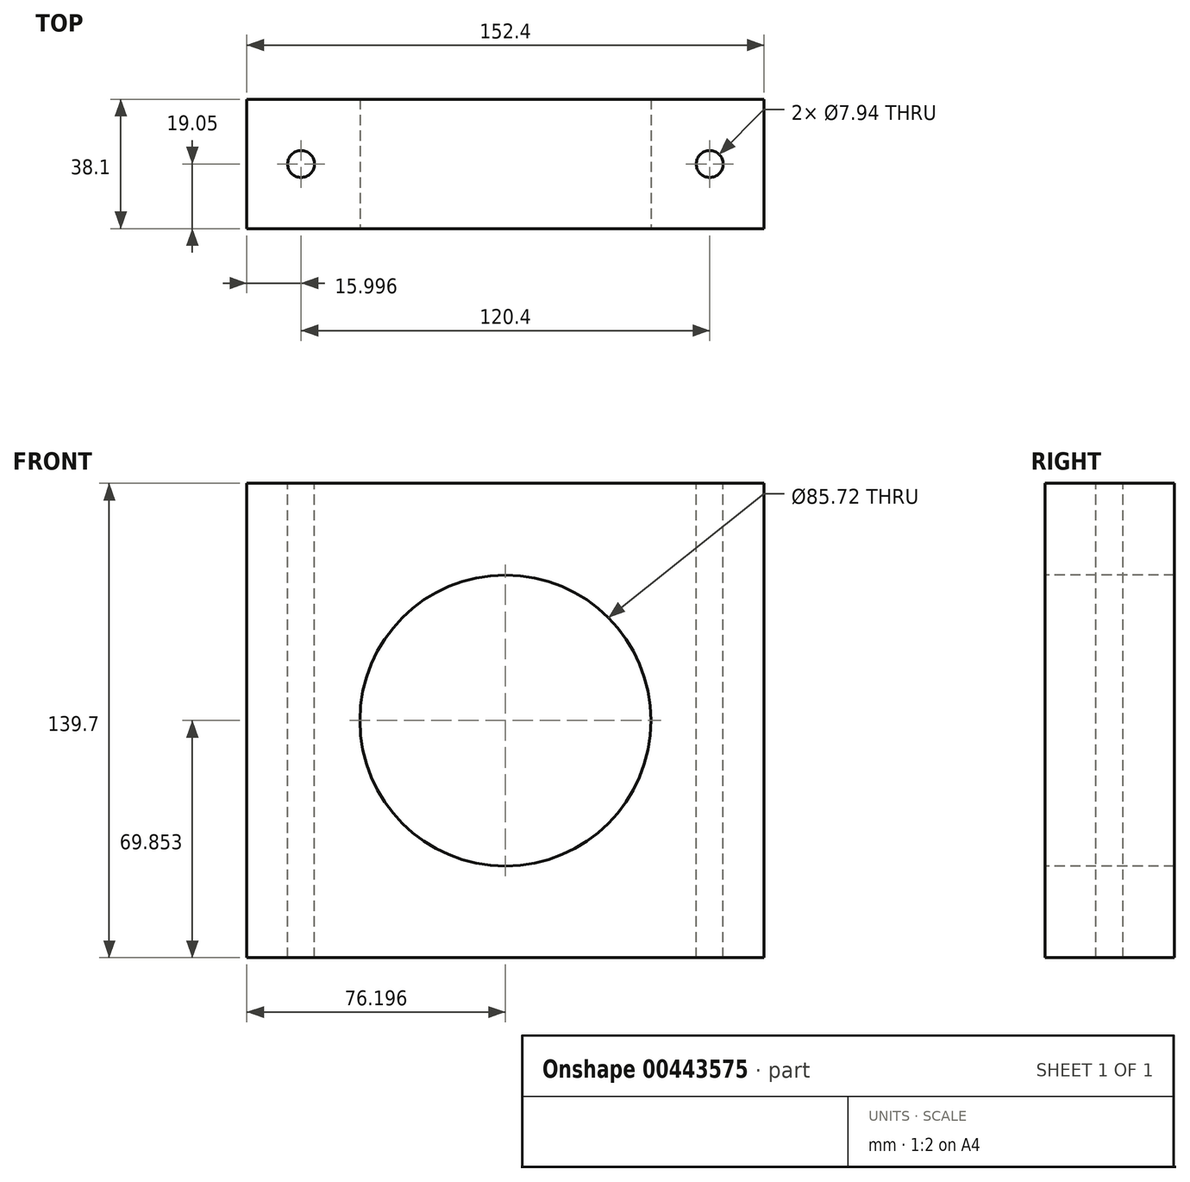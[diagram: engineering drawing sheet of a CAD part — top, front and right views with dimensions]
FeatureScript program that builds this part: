
annotation { "Feature Type Name" : "Feature", "Feature Type Description" : "" }
export const myFeature = defineFeature(function(context is Context, id is Id, definition is map)
    precondition{}
    {
        {
            var Q0;
            Q0=qCreatedBy(makeId("Front.planeOp"),FACE);
            var sketch = newSketch(context, id + "F0", { "sketchPlane" : qUnion([Q0])});
            skLineSegment(sketch, "E0.bottom", {"start": v(-104.36, 73.36) * mm, "end": v(48.04, 73.36) * mm});
            skLineSegment(sketch, "E0.top", {"start": v(-104.36, -66.34) * mm, "end": v(48.04, -66.34) * mm});
            skLineSegment(sketch, "E0.left", {"start": v(-104.36, 73.36) * mm, "end": v(-104.36, -66.34) * mm});
            skLineSegment(sketch, "E0.right", {"start": v(48.04, 73.36) * mm, "end": v(48.04, -66.34) * mm});
            skSolve(sketch);
        }
        {
            var Q0;
            Q0=makeQuery(id+"F0.imprint","IMPRINT",FACE,{"disambiguationData":[TD([[makeQuery(id+"F0.imprint","IMPRINT",EDGE,{"derivedFrom":sQuery(id+"F0.wireOp",EDGE,"E0.bottom")}),-1.0]])]});
            extrude(context, id + "F1", {"entities" : qUnion([Q0]), "depth" : (1.5 * 25.4) * mm});
        }
        {
            var Q0;
            Q0=makeQuery(id+"F1.opExtrude","CAP_FACE",FACE,{"disambiguationData":[OSD([sQuery(id+"F0.wireOp",EDGE,"E0.bottom"),sQuery(id+"F0.wireOp",EDGE,"E0.top"),sQuery(id+"F0.wireOp",EDGE,"E0.left"),sQuery(id+"F0.wireOp",EDGE,"E0.right")])],"isStart":false});
            var sketch = newSketch(context, id + "F2", { "sketchPlane" : qUnion([Q0])});
            skLineSegment(sketch, "E1", {"start": v(-28.16, 73.36) * mm, "end": v(-28.16, -66.34) * mm, "construction": true});
            skLineSegment(sketch, "E2", {"start": v(-104.36, 3.51) * mm, "end": v(48.04, 3.51) * mm, "construction": true});
            skCircle(sketch, "E3", {"center": v(-28.16, 3.51) * mm, "radius": 42.86 * mm});
            skSolve(sketch);
        }
        {
            var Q0;
            Q0 = qSketchRegion(id + "F2", true);
            extrude(context, id + "F3", {"entities" : qUnion([Q0]), "operationType" : NewBodyOperationType.REMOVE, "endBound" : BoundingType.THROUGH_ALL, "oppositeDirection" : true, "depth" : 25 * mm});
        }
        {
            var Q0;
            Q0=makeQuery(id+"F1.opExtrude","SWEPT_FACE",FACE,{"disambiguationData":[OSD([sQuery(id+"F0.wireOp",EDGE,"E0.bottom")])]});
            var sketch = newSketch(context, id + "F4", { "sketchPlane" : qUnion([Q0])});
            skLineSegment(sketch, "E4", {"start": v(-104.36, -19.05) * mm, "end": v(48.04, -19.05) * mm, "construction": true});
            skCircle(sketch, "E5", {"center": v(-88.36, -19.05) * mm, "radius": 3.97 * mm});
            skCircle(sketch, "E6", {"center": v(32.04, -19.05) * mm, "radius": 3.97 * mm});
            skSolve(sketch);
        }
        {
            var Q0;
            Q0 = qSketchRegion(id + "F4", true);
            extrude(context, id + "F5", {"entities" : qUnion([Q0]), "operationType" : NewBodyOperationType.REMOVE, "endBound" : BoundingType.THROUGH_ALL, "oppositeDirection" : true, "depth" : 25 * mm});
        }
    });
